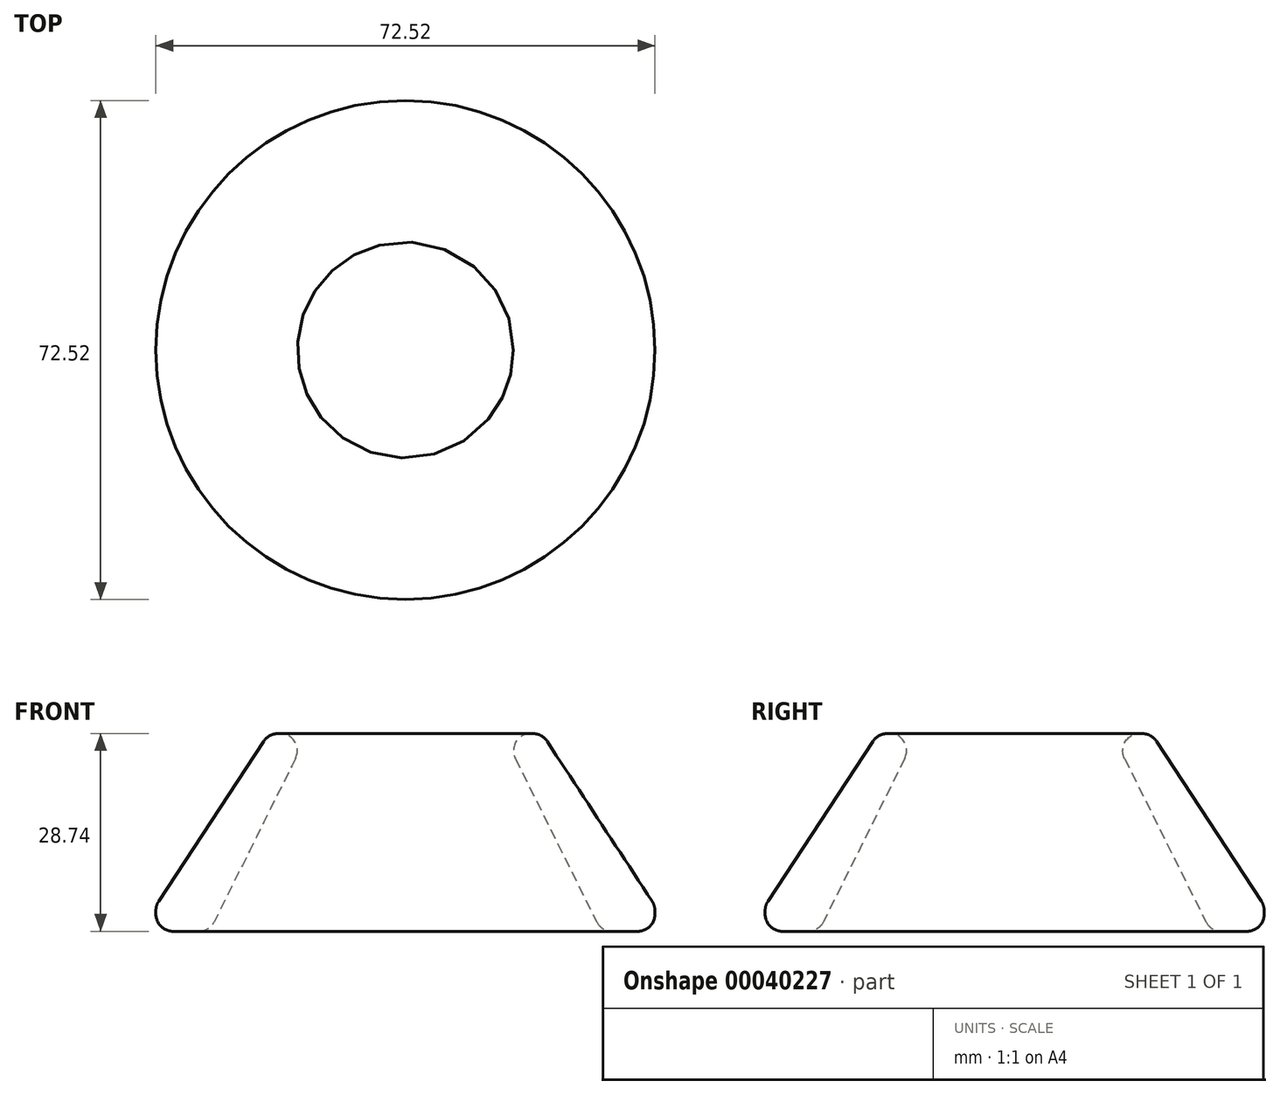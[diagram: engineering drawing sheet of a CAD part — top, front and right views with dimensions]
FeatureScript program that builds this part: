
annotation { "Feature Type Name" : "Feature", "Feature Type Description" : "" }
export const myFeature = defineFeature(function(context is Context, id is Id, definition is map)
    precondition{}
    {
        {
            var Q0;
            Q0=qCreatedBy(makeId("Front.planeOp"),FACE);
            var sketch = newSketch(context, id + "F0", { "sketchPlane" : qUnion([Q0])});
            skLineSegment(sketch, "E0", {"start": v(0, 0) * mm, "end": v(0, 37.66) * mm});
            skSolve(sketch);
        }
        {
            var Q0;
            Q0=qCreatedBy(makeId("Front.planeOp"),FACE);
            var sketch = newSketch(context, id + "F1", { "sketchPlane" : qUnion([Q0])});
            skLineSegment(sketch, "E1", {"start": v(-34.6, 21.2) * mm, "end": v(-34.6, 21.2) * mm});
            skLineSegment(sketch, "E2", {"start": v(-31.8, 24) * mm, "end": v(-31.8, 24) * mm});
            skLineSegment(sketch, "E3", {"start": v(-29, 21.2) * mm, "end": v(-29, 2.8) * mm});
            skLineSegment(sketch, "E4", {"start": v(-26.2, 0) * mm, "end": v(0, 0) * mm});
            skPoint(sketch, "E5.visualSharp", {"position": v(-34.6, 24) * mm});
            skArc(sketch, "E5.filletArc", {"start": v(-31.8, 24) * mm, "mid": v(-33.78, 23.18) * mm, "end": v(-34.6, 21.2) * mm});
            skPoint(sketch, "E6.visualSharp", {"position": v(-29, 24) * mm});
            skArc(sketch, "E6.filletArc", {"start": v(-29, 21.2) * mm, "mid": v(-29.82, 23.18) * mm, "end": v(-31.8, 24) * mm});
            skPoint(sketch, "E7.visualSharp", {"position": v(-29, 0) * mm});
            skArc(sketch, "E7.filletArc", {"start": v(-29, 2.8) * mm, "mid": v(-28.18, 0.82) * mm, "end": v(-26.2, 0) * mm});
            skSolve(sketch);
        }
        {
            var Q0;
            Q0=qCreatedBy(makeId("Front.planeOp"),FACE);
            var sketch = newSketch(context, id + "F2", { "sketchPlane" : qUnion([Q0])});
            skLineSegment(sketch, "E8", {"start": v(0, 54) * mm, "end": v(-9.16, 54) * mm});
            skLineSegment(sketch, "E9", {"start": v(-9.16, 54) * mm, "end": v(-108.37, 197.3) * mm});
            skSolve(sketch);
        }
        {
            var Q0;
            Q0=qCreatedBy(makeId("Front.planeOp"),FACE);
            var sketch = newSketch(context, id + "F3", { "sketchPlane" : qUnion([Q0])});
            skLineSegment(sketch, "E10", {"start": v(-28.47, 20.26) * mm, "end": v(-14.16, 49) * mm});
            skLineSegment(sketch, "E11", {"start": v(-28.47, 20.26) * mm, "end": v(-36.26, 20.26) * mm});
            skLineSegment(sketch, "E12", {"start": v(-36.26, 20.26) * mm, "end": v(-36.26, 24) * mm});
            skLineSegment(sketch, "E13", {"start": v(-36.26, 24) * mm, "end": v(-19.85, 49) * mm});
            skLineSegment(sketch, "E14", {"start": v(-19.85, 49) * mm, "end": v(-14.16, 49) * mm});
            skSolve(sketch);
        }
        {
            var Q0;
            Q0=makeQuery(id+"F3.imprint","IMPRINT",FACE,{"disambiguationData":[TD([[makeQuery(id+"F3.imprint","IMPRINT",EDGE,{"derivedFrom":sQuery(id+"F3.wireOp",EDGE,"E10")}),1.0]])]});
            var Q1;
            Q1=sQuery(id+"F3.wireOp",EDGE,"E10");
            var Q2;
            Q2=sQuery(id+"F0.wireOp",EDGE,"E0");
            revolve(context, id + "F4", {"entities" : qUnion([Q0]), "surfaceEntities" : qUnion([Q1]), "axis" : qUnion([Q2]), "revolveType" : RevolveType.FULL});
        }
        {
            var Q0;
            Q0=makeQuery(id+"F4.opRevolve","SWEPT_EDGE",EDGE,{"disambiguationData":[OSD([sQuery(id+"F3.wireOp",EDGE,"E13"),sQuery(id+"F3.wireOp",EDGE,"E14")])]});
            var Q1;
            Q1=makeQuery(id+"F4.opRevolve","SWEPT_EDGE",EDGE,{"disambiguationData":[OSD([sQuery(id+"F3.wireOp",EDGE,"E10"),sQuery(id+"F3.wireOp",EDGE,"E14")])]});
            var Q2;
            Q2=makeQuery(id+"F4.opRevolve","SWEPT_EDGE",EDGE,{"disambiguationData":[OSD([sQuery(id+"F3.wireOp",EDGE,"E12"),sQuery(id+"F3.wireOp",EDGE,"E13")])]});
            var Q3;
            Q3=makeQuery(id+"F4.opRevolve","SWEPT_EDGE",EDGE,{"disambiguationData":[OSD([sQuery(id+"F3.wireOp",EDGE,"E11"),sQuery(id+"F3.wireOp",EDGE,"E12")])]});
            var Q4;
            Q4=makeQuery(id+"F4.opRevolve","SWEPT_EDGE",EDGE,{"disambiguationData":[OSD([sQuery(id+"F3.wireOp",EDGE,"E10"),sQuery(id+"F3.wireOp",EDGE,"E11")])]});
            fillet(context, id + "F5", {"entities" : qUnion([Q0, Q1, Q2, Q3, Q4]), "radius" : 2.5 * mm, "tangentPropagation" : true, "allowEdgeOverflow" : false});
        }
        {
            var Q0;
            Q0=sQuery(id+"F1.wireOp",EDGE,"E5.filletArc");
            var Q1;
            Q1=sQuery(id+"F1.wireOp",EDGE,"E6.filletArc");
            var Q2;
            Q2=sQuery(id+"F1.wireOp",EDGE,"E3");
            var Q3;
            Q3=sQuery(id+"F1.wireOp",EDGE,"E7.filletArc");
            var Q4;
            Q4=sQuery(id+"F1.wireOp",EDGE,"E4");
            var Q5;
            Q5=sQuery(id+"F2.wireOp",EDGE,"E9");
            var Q6;
            Q6=sQuery(id+"F0.wireOp",EDGE,"E0");
            revolve(context, id + "F6", {"bodyType" : ToolBodyType.SURFACE, "surfaceEntities" : qUnion([Q0, Q1, Q2, Q3, Q4, Q5]), "axis" : qUnion([Q6]), "revolveType" : RevolveType.FULL});
        }
    });
